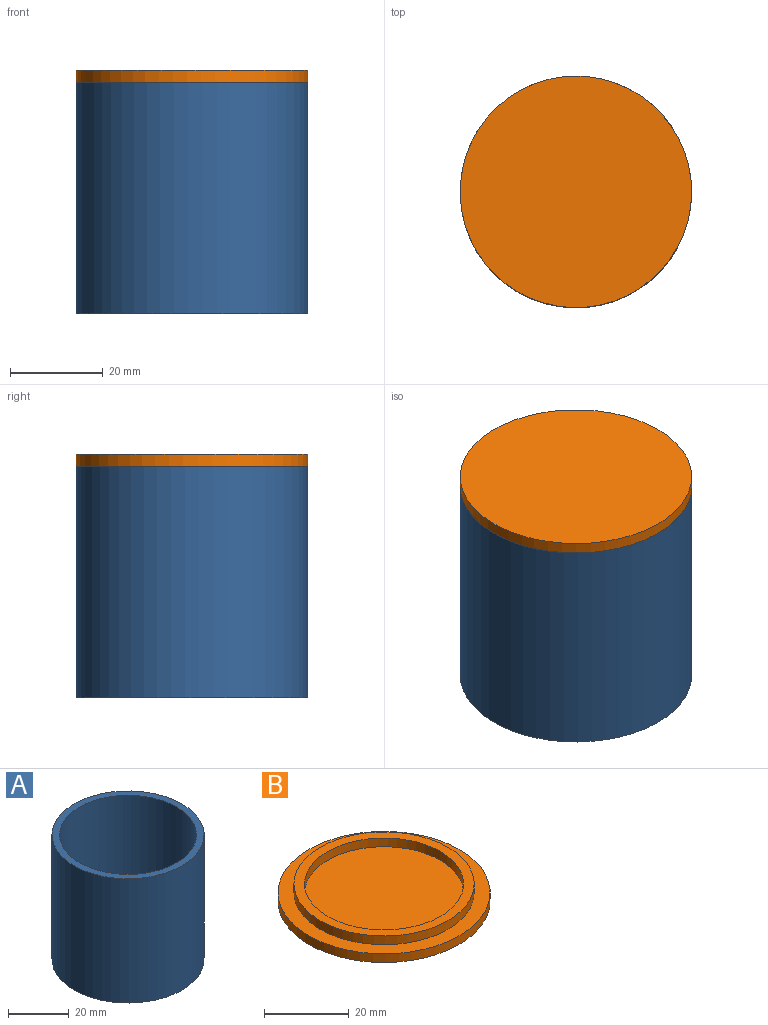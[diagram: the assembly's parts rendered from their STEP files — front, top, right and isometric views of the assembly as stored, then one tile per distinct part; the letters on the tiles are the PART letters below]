
ASSEMBLY  parts=2 mates=1
PART A: 5 faces, bbox 50x50x50 mm
  f0: plane 45x45mm, normal (0,0,1), area 1590.4mm2, adj f1
  f1: cylinder r=22.5mm len=47.5mm, axis (0,0,-1), area 6715.2mm2, adj f0,f3
  f2: cylinder r=25mm len=50mm, axis (0,0,-1), area 7854mm2, adj f3,f4
  f3: plane 50x50mm, normal (0,0,1), area 373.1mm2, adj f1,f2
  f4: plane 50x50mm, normal (0,0,-1), area 1963.5mm2, adj f2
PART B: 7 faces, bbox 50x50x5 mm
  f0: cylinder r=25mm len=50mm, axis (0,0,-1), area 392.7mm2, adj f1,f2
  f1: plane 50x50mm, normal (0,0,1), area 544.9mm2, adj f0,f3
  f2: plane 50x50mm, normal (0,0,-1), area 1963.5mm2, adj f0
  f3: cylinder r=21.25mm len=42.5mm, axis (0,0,-1), area 333.8mm2, adj f1,f6
  f4: plane 37.5x37.5mm, normal (0,0,1), area 1104.5mm2, adj f5
  f5: cylinder r=18.75mm len=37.5mm, axis (0,0,-1), area 294.5mm2, adj f4,f6
  f6: plane 42.5x42.5mm, normal (0,0,1), area 314.2mm2, adj f3,f5
PLACE A t=(-42.9,5.23,8.55)mm fixed
PLACE B rot(axis=(0.81,-0.58,0),180deg) t=(-42.9,5.23,61.05)mm
MATE cylindrical B.f0 <-> A.f1  axis (0,0,-1) through (-42.9,5.23,58.55)mm
